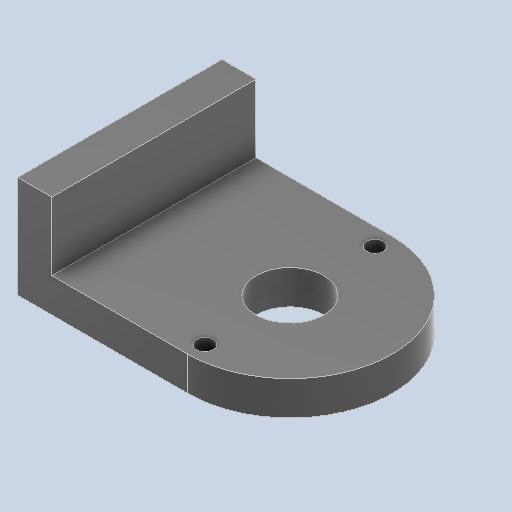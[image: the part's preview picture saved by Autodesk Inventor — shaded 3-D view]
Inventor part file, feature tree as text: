
AUTODESK INVENTOR PART (.ipt)
format: ipt  version: 2022 (Build 260153000, 153)  size: 154,624 bytes
history: native  units: in
note: dims shown in document units (in); Inventor stores cm internally (conversion verified against a paired STEP export)
features: extrude x2, sketch x2
ambient origin geometry x8: Origin, YZ Plane, XZ Plane, XY Plane, X Axis, Y Axis, Z Axis, Center Point
bodies: Solid1 (feature_tree)
feature tree (4):
  extrude  "Extrusion1"  Depth=0.125in
  extrude  "Extrusion2"  Depth=1.5in
  sketch  "Sketch1"  dims[d0=0.125in d1=0.125in]
  sketch  "Sketch2"  dims[d2=0.125in d3=0.125in d4=1.5in d5=0.75in d6=0.5in d8=0.75in d9=0.5in d10=0.25in d11=0.25in d12=0.0in d13=0.5in d14=0.0in d16=0.25in d17=1.5in]
